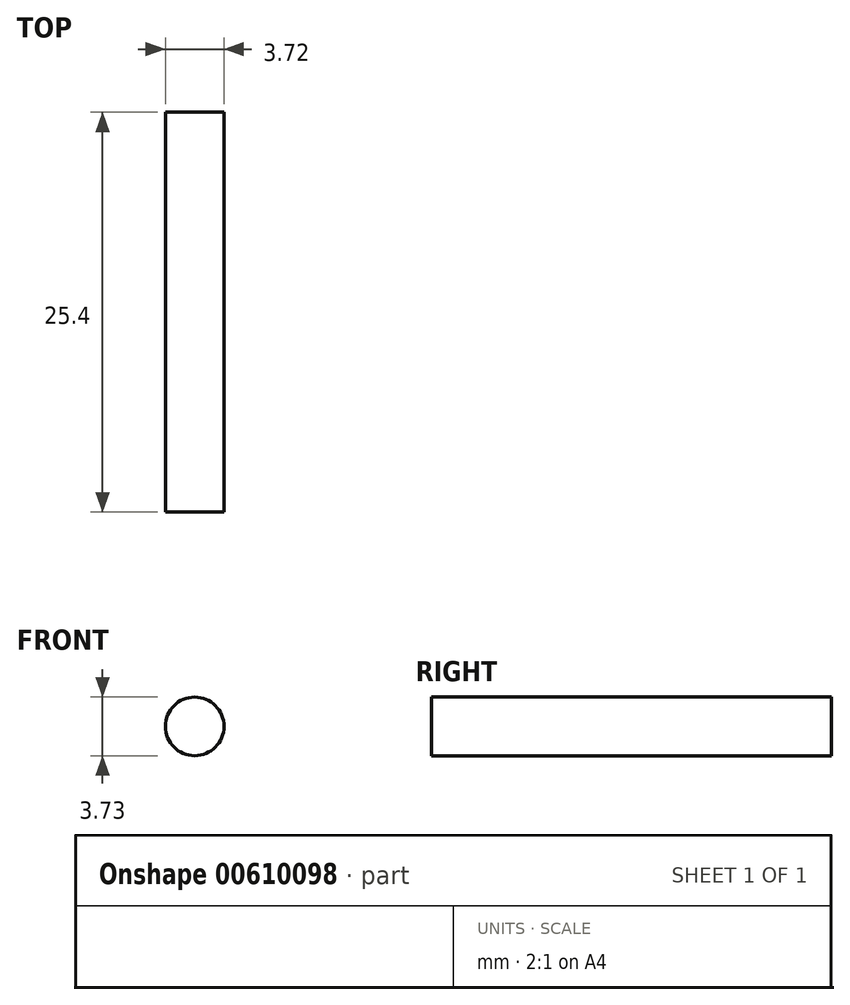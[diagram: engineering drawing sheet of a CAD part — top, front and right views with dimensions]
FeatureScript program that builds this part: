
annotation { "Feature Type Name" : "Feature", "Feature Type Description" : "" }
export const myFeature = defineFeature(function(context is Context, id is Id, definition is map)
    precondition{}
    {
        {
            var Q0;
            Q0=qCreatedBy(makeId("Front.planeOp"),FACE);
            var sketch = newSketch(context, id + "F0", { "sketchPlane" : qUnion([Q0])});
            skCircle(sketch, "E0", {"center": v(-44.35, 21.86) * mm, "radius": 1.86 * mm});
            skSolve(sketch);
        }
        {
            var Q0;
            Q0 = qSketchRegion(id + "F0", true);
            extrude(context, id + "F1", {"entities" : qUnion([Q0]), "depth" : 25.4 * mm, "offsetDistance" : 25.4 * mm});
        }
    });
